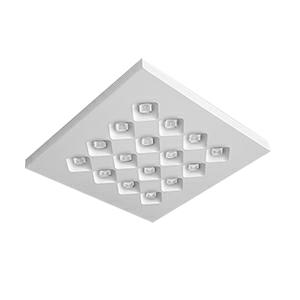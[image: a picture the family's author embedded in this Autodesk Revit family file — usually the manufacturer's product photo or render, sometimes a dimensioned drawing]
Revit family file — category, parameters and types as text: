
# Revit family: 3f_filippi_-_3f_diagon_3f_filippi_-_23029_a0686_-_3f_diagon_15w-840_dali_596x596___corn_plaf__a48b
name_source: partatom
category: Lighting Fixtures
units: mm (PartAtom-declared; Revit-internal decimal feet)

## family parameters
Cut with Voids When Loaded = No
Host = Face
Light Source = No
Part Type = Normal
Room Calculation Point = No
Round Connector Dimension = Use Diameter
Shared = No

## types (1)
- 3F Filippi - 3F Dìagon (1 x LED, 2694 lm, 17 W, 4000 K)
    Apparent Load = 17 VA
    Approval mark = CE
    CIE Flux Codes = 67 96 100 100 100
    Color Rendering = 80
    Color Temperature = 4000 K
    Control Gear = Electronic transformer
    Default Elevation = 1800 mm
    Description = ILLUMINOTECHNICAL
Luminous efficiency 100% (DLOR 100%, ULOR 0%).
Initial luminous flux of the luminaire 2694 lm.
Direct symmetric distribution.
Installation Interdistance Transv.D = 1.39 x hu - Long.D = 1.39 x hu.
Average luminance <1000 cd/m² for radial angles >65°.
Tabular UGR (CIE 117 - 4H-8H; S=0.25H; 70/50/20): RUG 15.8 - 15.7.
Beam angle: 93° - 92°.
Luminous efficacy 158 lm/W.
Lifetime (L95/B10): 30000 h. (tq+25°C)
Lifetime (L90/B10): 50000 h. (tq+25°C)
Lifetime (L80/B10): 80000 h. (tq+25°C)
Lifetime (L75/B10): 100000 h. (tq+25°C)
Sudden decreased luminous flux after 50000 hours: 0% (C0).
Photobiological safety in compliance with IEC/TR 62778: RG0 risk exempt, (IEC 62471).
In compliance with IEC/EN 62722-2-1 - IEC/EN 62717 standards.

SOURCE
Squared LED module 15W/840.
Energy efficiency class (UE 2019/2020 - UE 2019/2015): C.
CIE 13.3 Colour rendering index: CRI >80 (R9 <50%).
IES TM-30 Fidelity Index: Rf = 84 Rg = 95.
CCT nominal colour temperature 4000 K.
Colour initial tolerance (MacAdam): SDCM 3.

MECHANICAL
Housing in hot-galvanised steel, painted in white polyester.
Honeycombed diagonal screen in white anti-glare polycarbonate.
Rhomboidal lenses with differentiated surfaces, etched and prismatic to optimise the orientation of the luminous flux, in transparent methacrylate (PMMA).
Luminaire with limited surface temperature. - D - (EN 60598-2-24)
Dimensions: 600x600 mm, height 40 mm. Weight 6.16 kg.
IP43 protection degree for exposed part, IP20 for recessed part.
Mechanical strength to impacts IK06 (1 joule).
Glow-wire test resistance 650°C.

ELECTRICAL
Halogen Free DALI-2, PUSH-DIM, electronic wiring 230V-50/60Hz, power factor 0.95 at full load, THD <25%, constant output current, class I, 1 driver, 1 DALI addresse.
Power of the luminaire 17 W.
ENEC - CE.
SAFE FLICKER: PstLM=<1 and SVM=<0.4 (IEC TR 61547-1 and IEC TR 63158), to ensure a more comfortable and safe light.
Luminaire compliant with EN 60598-2-22 for power supply from a centralised emergency system CPSS (Central Power Supply System), not incorporated in the luminaire - high risk areas excluded. The default power and flux are 100% in AC and 15% in DC.
Ambient temperature from 0°C to +25°C.
Temperature class T6 max 85°C.
Quick connection.
Relative humidity UR: <85%.

INSTALLATION
Ceiling.
Height only 40 mm.
All accessories dedicated to this product are available on the Catalog and on our website www.3F-Filippi.com.

ACCESSORIES
A0686 - 596x596 Diagon frame for Ceiling installation.

APPLICATIONS
Environments: staterooms, with VDTs, offices.
Environments with exacting visual tasks, where diffused soft light for optimum visual comfort is required.

LIGHT MANAGEMENT
Recommended minimum setting: 10%.
The device, equipped with DALI-2 driver, can be controlled manually with 3F Easy Dim technology or automatically/manually with 3F Smart Dimming technology and/or centralised DALI systems.
DALI-2 certification guarantees interoperability with other devices with the same certification.
In electrical systems without a regulation system (manual or automatic) and DALI bus, a suitable jumper must be made on the DA-DA terminals of the appliance.

WARNING
Luminaire designed for disposal/recycling at end-of-life.
Replaceable (LED only) light source by a professional. Replaceable control gear by a professional.
    Height = 0 mm  [stored 0 ft]
    Lamp = 1 x LED
    Lamp Light Flux = 2694 lm
    Lamp Power = 17 W
    Lamp count = 1
    Length = 600 mm
    Lifetime = 50000 h
    Luminous efficacy = 158 lm/W
    Manufacturer = 3F Filippi
    ModVariant = No
    Model = 3F Filippi - 23029+A0686 - 3F Diagon 15W-840 DALI 596x596 + Corn.plaf.
    Mounting Place = Ceiling
    Mounting Type = Recessed
    Number of Poles = 1
    OnlyDefault = Yes
    Power Factor = 1
    Product Name = 3F Filippi - 3F Dìagon
    Product group = recessed luminaire
    ProductGroupID = 4
    Protection Class = Protection class I
    Protection Degree = IP 20
    RLX_Detail_Level = 1
    RLX_Emergency_Light_Flux = 0 lm
    RLX_Emergency_Type = 0
    RLX_Emergency_Type_DB = No
    RlxData = <blob elided: 98029 chars, md5=43a4dd68>
    Socket = socket
    Standby Power = 0 W
    System Light Flux = 2694 lm
    System Power = 17 W
    Type Comments = Product without accessories
    Type Image = 3ffilippi_3f_diagon__a0686.jpg
    URL = http://relux.com
    VarID = ---
    Voltage = 0 V
    Weight = 0.00 kg
    Width = 600 mm

note: [stored X ft] marks values corroborated as IEEE doubles in the binary element streams (Revit-internal decimal feet)

## geometry (parser evidence)
native form markers: Blend x4, Sweep x8
no freeform markers — native parametric forms only
